# Revit family: Sanitary_Accessories_hansgrohe_27671000-Rainfinity-Shower-set-130-3jet__
name_source: partatom
category: Plumbing Fixtures
revit_build: Autodesk Revit 2015 (Build: 20140903_1530(x64)
units: mm (PartAtom-declared; Revit-internal decimal feet)

## types (1)
- Chrome 000
    BIMobject category = Showers
    BIMobject category code = sanitary-showers
    BIMobject main category = Sanitary
    BIMobject main category code = sanitary
    BOSUseNativeGeometries = 1
    Brand url = http://www.hansgrohe-int.com
    Default Elevation = 4' - 0"
    Design country = Germany
    Edition number = 1
    GTIN code = https://4059625214145
    IFC Classification = Sanitary Terminal
    Installation instructions = https://www.hansgrohe.com
    Manufacturer country = Germany
    Manufacturer name = hansgrohe
    Masterformat 2014 Code = 22 41 23
    Masterformat 2014 Description = Residential Showers
    Material main = Chrome
    Material secondary = Chrome
    NBS Reference Code = 35-06-81
    NBS Reference Description = Shower Heads
    Nominal height = 0' - 0"
    Nominal width = 0' - 0"
    Product Guid = 54329dd1-decc-45fa-9c46-ba74301dc9df
    Product SKU = 27671000
    Product data url = https://bimobject.com
    Product family = Rainfinity
    Product group = Wallbar sets
    Product url = https://www.hansgrohe.com
    QR code = http://bimobject.com
    Technical description = https://www.hansgrohe.com
    UNSPSC Code = 30181503
    Uniclass 1.4 Code = L7214
    Uniclass 1.4 Description = Showers
    Uniclass 2.0 Code = PR-35-06-81
    Uniclass 2.0 Description = Shower Heads
    Uniclass 2015 Code = SL_35_80_80
    Uniclass 2015 Name = Showers
    Uniformat II Code = D2010
    Uniformat II Description = Plumbing Fixtures
    Weight Net (Kg) = 2.9

## geometry (parser evidence)
native form markers: Blend x2, Sweep x2
no freeform markers — native parametric forms only
